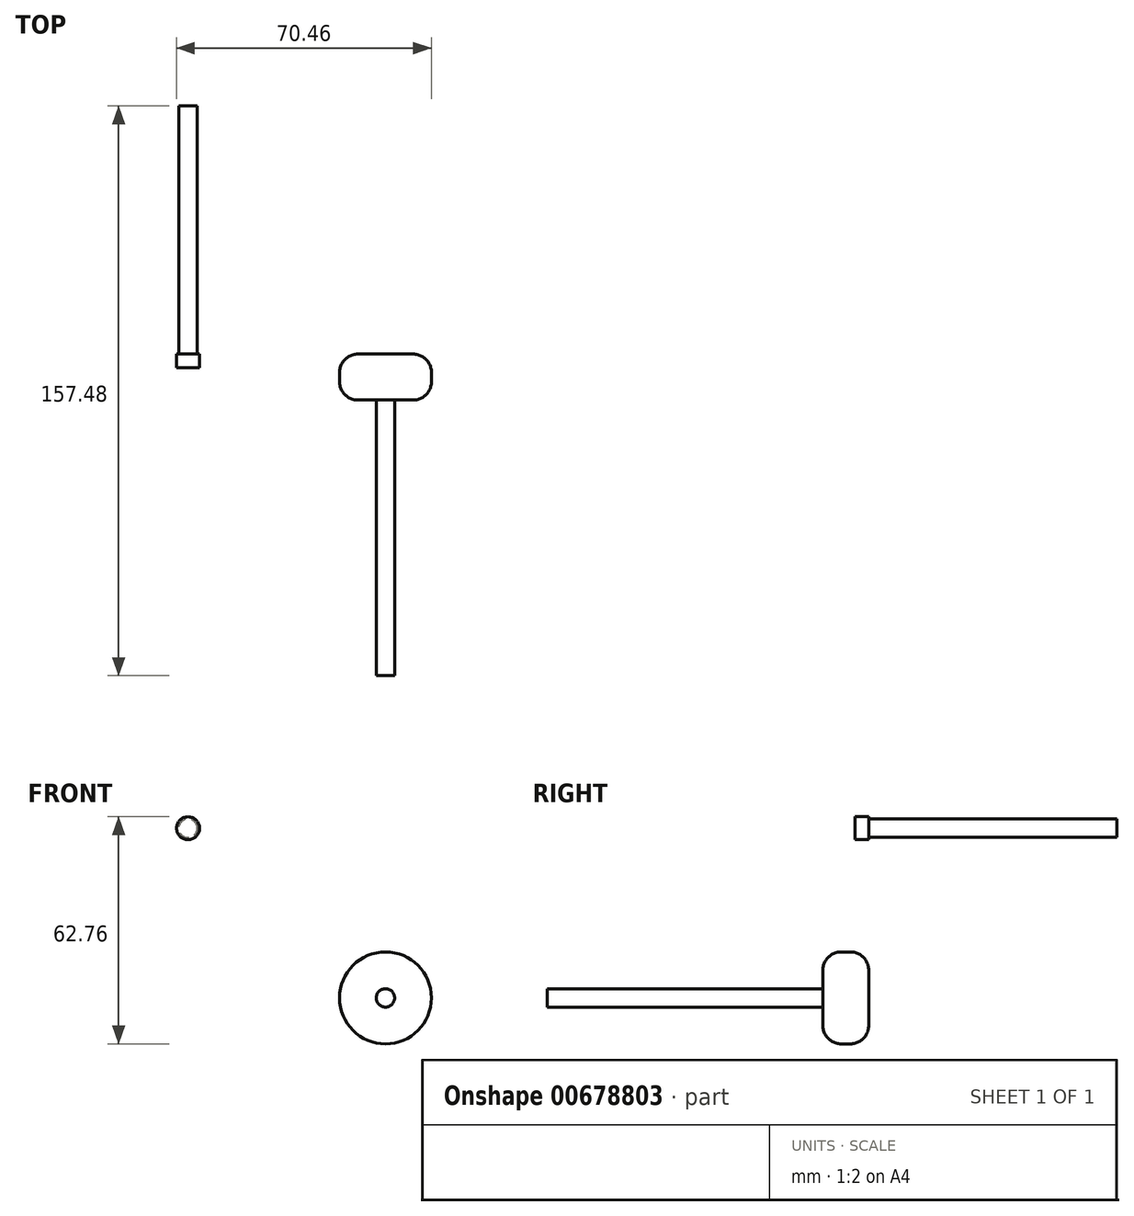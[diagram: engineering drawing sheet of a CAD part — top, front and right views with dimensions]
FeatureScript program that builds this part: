
annotation { "Feature Type Name" : "Feature", "Feature Type Description" : "" }
export const myFeature = defineFeature(function(context is Context, id is Id, definition is map)
    precondition{}
    {
        {
            var Q0;
            Q0=qCreatedBy(makeId("Front.planeOp"),FACE);
            var sketch = newSketch(context, id + "F0", { "sketchPlane" : qUnion([Q0])});
            skCircle(sketch, "E0", {"center": v(0, 0) * mm, "radius": 12.7 * mm});
            skSolve(sketch);
        }
        {
            var Q0;
            Q0 = qSketchRegion(id + "F0", true);
            extrude(context, id + "F1", {"entities" : qUnion([Q0]), "depth" : 12.7 * mm, "offsetDistance" : 25.4 * mm});
        }
        {
            var Q0;
            Q0=makeQuery(id+"F1.opExtrude","CAP_FACE",FACE,{"disambiguationData":[OSD([sQuery(id+"F0.wireOp",EDGE,"E0")])],"isStart":false});
            var sketch = newSketch(context, id + "F2", { "sketchPlane" : qUnion([Q0])});
            skCircle(sketch, "E1", {"center": v(0, 0) * mm, "radius": 2.54 * mm});
            skSolve(sketch);
        }
        {
            var Q0;
            Q0 = qSketchRegion(id + "F2", true);
            extrude(context, id + "F3", {"entities" : qUnion([Q0]), "operationType" : NewBodyOperationType.ADD, "depth" : 76.2 * mm, "offsetDistance" : 25.4 * mm});
        }
        {
            var Q0;
            Q0=makeQuery(id+"F1.opExtrude","CAP_EDGE",EDGE,{"disambiguationData":[OSD([sQuery(id+"F0.wireOp",EDGE,"E0")])],"isStart":false});
            var Q1;
            Q1=makeQuery(id+"F1.opExtrude","CAP_EDGE",EDGE,{"disambiguationData":[OSD([sQuery(id+"F0.wireOp",EDGE,"E0")])],"isStart":true});
            fillet(context, id + "F4", {"entities" : qUnion([Q0, Q1]), "radius" : 5.08 * mm, "tangentPropagation" : true, "allowEdgeOverflow" : false});
        }
        {
            var Q0;
            Q0=qCreatedBy(makeId("Front.planeOp"),FACE);
            var sketch = newSketch(context, id + "F5", { "sketchPlane" : qUnion([Q0])});
            skCircle(sketch, "E2", {"center": v(-54.59, 46.88) * mm, "radius": 3.18 * mm});
            skSolve(sketch);
        }
        {
            var Q0;
            Q0 = qSketchRegion(id + "F5", true);
            extrude(context, id + "F6", {"entities" : qUnion([Q0]), "depth" : 3.8 * mm, "offsetDistance" : 25.4 * mm});
        }
        {
            var Q0;
            Q0=makeQuery(id+"F6.opExtrude","CAP_FACE",FACE,{"disambiguationData":[OSD([sQuery(id+"F5.wireOp",EDGE,"E2")])],"isStart":true});
            var sketch = newSketch(context, id + "F7", { "sketchPlane" : qUnion([Q0])});
            skCircle(sketch, "E3", {"center": v(54.59, 46.88) * mm, "radius": 2.54 * mm});
            skSolve(sketch);
        }
        {
            var Q0;
            Q0 = qSketchRegion(id + "F7", true);
            extrude(context, id + "F8", {"entities" : qUnion([Q0]), "operationType" : NewBodyOperationType.ADD, "depth" : 68.58 * mm, "offsetDistance" : 25.4 * mm});
        }
    });
